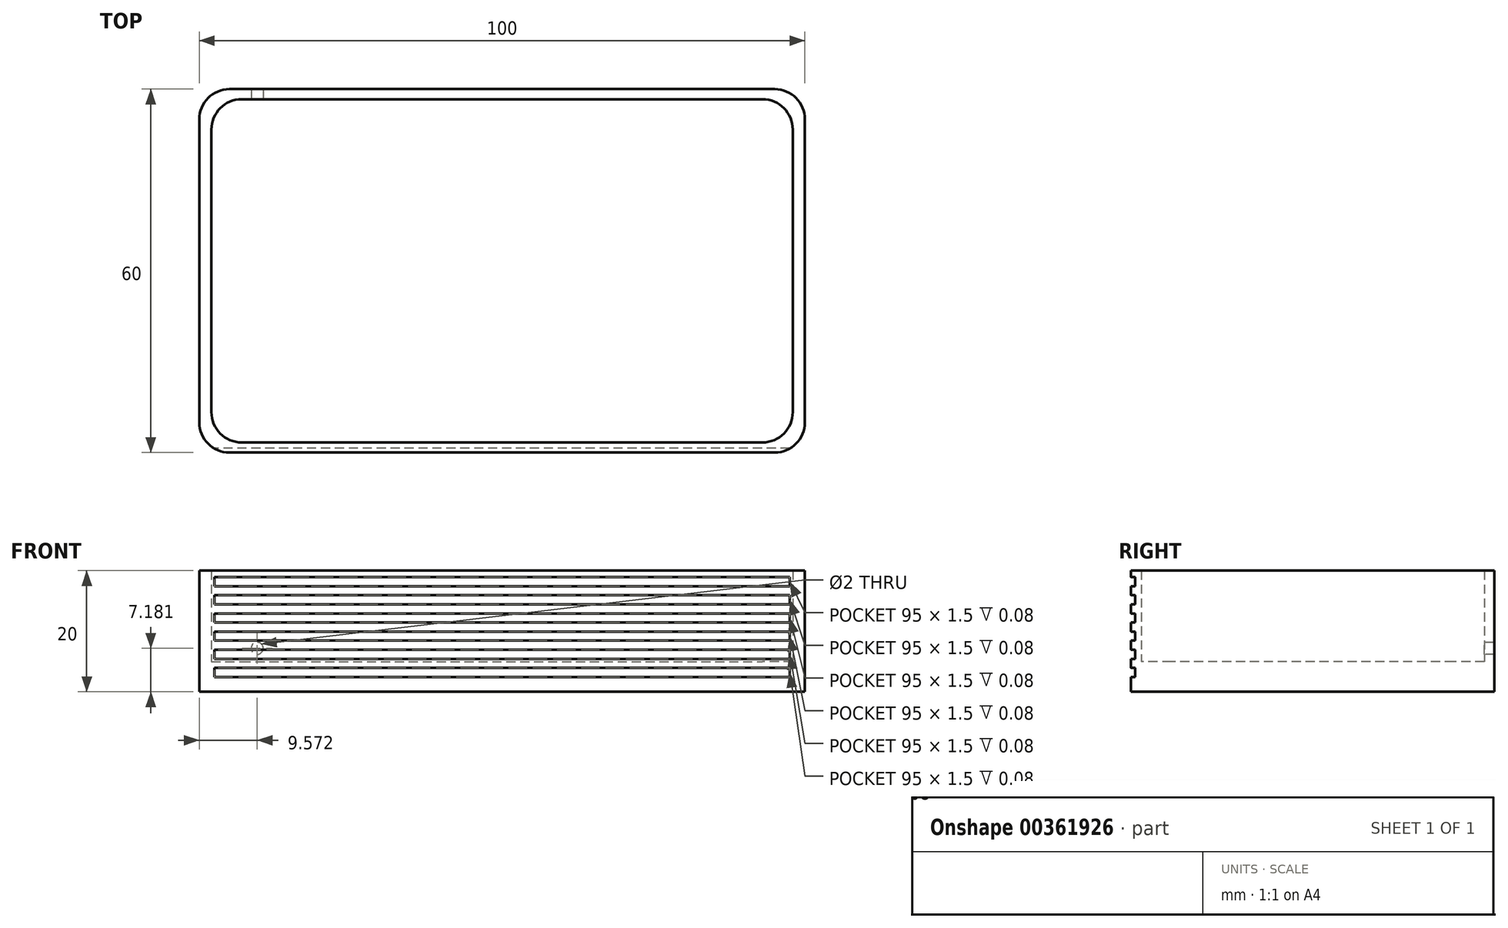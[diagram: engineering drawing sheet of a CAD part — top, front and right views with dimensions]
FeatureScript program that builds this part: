
annotation { "Feature Type Name" : "Feature", "Feature Type Description" : "" }
export const myFeature = defineFeature(function(context is Context, id is Id, definition is map)
    precondition{}
    {
        {
            var Q0;
            Q0=qCreatedBy(makeId("Top.planeOp"),FACE);
            var sketch = newSketch(context, id + "F0", { "sketchPlane" : qUnion([Q0])});
            skPoint(sketch, "E0.middle", {"position": v(0, 0) * mm});
            skLineSegment(sketch, "E1.bottom", {"start": v(45, -30) * mm, "end": v(-45, -30) * mm});
            skLineSegment(sketch, "E1.top", {"start": v(45, 30) * mm, "end": v(-45, 30) * mm});
            skLineSegment(sketch, "E1.left", {"start": v(50, -25) * mm, "end": v(50, 25) * mm});
            skLineSegment(sketch, "E1.right", {"start": v(-50, -25) * mm, "end": v(-50, 25) * mm});
            skLineSegment(sketch, "E2.bottom", {"start": v(-43, 28.33) * mm, "end": v(43, 28.33) * mm});
            skLineSegment(sketch, "E2.top", {"start": v(-43, -28.33) * mm, "end": v(43, -28.33) * mm});
            skLineSegment(sketch, "E2.left", {"start": v(-48, 23.33) * mm, "end": v(-48, -23.33) * mm});
            skLineSegment(sketch, "E2.right", {"start": v(48, 23.33) * mm, "end": v(48, -23.33) * mm});
            skPoint(sketch, "E3.visualSharp", {"position": v(-48, 28.33) * mm});
            skArc(sketch, "E3.filletArc", {"start": v(-43, 28.33) * mm, "mid": v(-46.54, 26.86) * mm, "end": v(-48, 23.33) * mm});
            skPoint(sketch, "E4.visualSharp", {"position": v(-50, 30) * mm});
            skArc(sketch, "E4.filletArc", {"start": v(-45, 30) * mm, "mid": v(-48.54, 28.54) * mm, "end": v(-50, 25) * mm});
            skPoint(sketch, "E5.visualSharp", {"position": v(-48, -28.33) * mm});
            skArc(sketch, "E5.filletArc", {"start": v(-48, -23.33) * mm, "mid": v(-46.54, -26.86) * mm, "end": v(-43, -28.33) * mm});
            skPoint(sketch, "E6.visualSharp", {"position": v(-50, -30) * mm});
            skArc(sketch, "E6.filletArc", {"start": v(-50, -25) * mm, "mid": v(-48.54, -28.54) * mm, "end": v(-45, -30) * mm});
            skPoint(sketch, "E7.visualSharp", {"position": v(48, -28.33) * mm});
            skArc(sketch, "E7.filletArc", {"start": v(43, -28.33) * mm, "mid": v(46.54, -26.86) * mm, "end": v(48, -23.33) * mm});
            skPoint(sketch, "E8.visualSharp", {"position": v(50, -30) * mm});
            skArc(sketch, "E8.filletArc", {"start": v(45, -30) * mm, "mid": v(48.54, -28.54) * mm, "end": v(50, -25) * mm});
            skPoint(sketch, "E9.visualSharp", {"position": v(50, 30) * mm});
            skArc(sketch, "E9.filletArc", {"start": v(50, 25) * mm, "mid": v(48.54, 28.54) * mm, "end": v(45, 30) * mm});
            skPoint(sketch, "E10.visualSharp", {"position": v(48, 28.33) * mm});
            skArc(sketch, "E10.filletArc", {"start": v(48, 23.33) * mm, "mid": v(46.54, 26.86) * mm, "end": v(43, 28.33) * mm});
            skSolve(sketch);
        }
        {
            var Q0;
            Q0=makeQuery(id+"F0.imprint","IMPRINT",FACE,{"disambiguationData":[TD([[makeQuery(id+"F0.imprint","IMPRINT",EDGE,{"derivedFrom":sQuery(id+"F0.wireOp",EDGE,"E1.bottom")}),-1.0]])]});
            extrude(context, id + "F1", {"entities" : qUnion([Q0]), "depth" : 20 * mm});
        }
        {
            var Q0;
            Q0=makeQuery(id+"F0.imprint","IMPRINT",FACE,{"disambiguationData":[TD([[makeQuery(id+"F0.imprint","IMPRINT",EDGE,{"derivedFrom":sQuery(id+"F0.wireOp",EDGE,"E2.bottom")}),-1.0]])]});
            extrude(context, id + "F2", {"entities" : qUnion([Q0]), "operationType" : NewBodyOperationType.ADD, "depth" : 5 * mm});
        }
        {
            var Q0;
            Q0=makeQuery(id+"F1.opExtrude","SWEPT_FACE",FACE,{"disambiguationData":[OSD([sQuery(id+"F0.wireOp",EDGE,"E1.bottom")])]});
            var sketch = newSketch(context, id + "F3", { "sketchPlane" : qUnion([Q0])});
            skLineSegment(sketch, "E11.bottom", {"start": v(47.5, 2.45) * mm, "end": v(-47.5, 2.45) * mm});
            skLineSegment(sketch, "E11.top", {"start": v(47.5, 3.95) * mm, "end": v(-47.5, 3.95) * mm});
            skLineSegment(sketch, "E11.left", {"start": v(47.5, 2.45) * mm, "end": v(47.5, 3.95) * mm});
            skLineSegment(sketch, "E11.right", {"start": v(-47.5, 2.45) * mm, "end": v(-47.5, 3.95) * mm});
            skPoint(sketch, "E11.middle", {"position": v(0, 3.2) * mm});
            skLineSegment(sketch, "E12.0.1.0", {"start": v(-47.5, 5.45) * mm, "end": v(-47.5, 6.95) * mm});
            skLineSegment(sketch, "E12.0.1.1", {"start": v(47.5, 5.45) * mm, "end": v(-47.5, 5.45) * mm});
            skLineSegment(sketch, "E12.0.1.2", {"start": v(47.5, 6.95) * mm, "end": v(-47.5, 6.95) * mm});
            skLineSegment(sketch, "E12.0.1.3", {"start": v(47.5, 5.45) * mm, "end": v(47.5, 6.95) * mm});
            skLineSegment(sketch, "E12.0.2.0", {"start": v(-47.5, 8.45) * mm, "end": v(-47.5, 9.95) * mm});
            skLineSegment(sketch, "E12.0.2.1", {"start": v(47.5, 8.45) * mm, "end": v(-47.5, 8.45) * mm});
            skLineSegment(sketch, "E12.0.2.2", {"start": v(47.5, 9.95) * mm, "end": v(-47.5, 9.95) * mm});
            skLineSegment(sketch, "E12.0.2.3", {"start": v(47.5, 8.45) * mm, "end": v(47.5, 9.95) * mm});
            skLineSegment(sketch, "E12.0.3.0", {"start": v(-47.5, 11.45) * mm, "end": v(-47.5, 12.95) * mm});
            skLineSegment(sketch, "E12.0.3.1", {"start": v(47.5, 11.45) * mm, "end": v(-47.5, 11.45) * mm});
            skLineSegment(sketch, "E12.0.3.2", {"start": v(47.5, 12.95) * mm, "end": v(-47.5, 12.95) * mm});
            skLineSegment(sketch, "E12.0.3.3", {"start": v(47.5, 11.45) * mm, "end": v(47.5, 12.95) * mm});
            skLineSegment(sketch, "E12.0.4.0", {"start": v(-47.5, 14.45) * mm, "end": v(-47.5, 15.95) * mm});
            skLineSegment(sketch, "E12.0.4.1", {"start": v(47.5, 14.45) * mm, "end": v(-47.5, 14.45) * mm});
            skLineSegment(sketch, "E12.0.4.2", {"start": v(47.5, 15.95) * mm, "end": v(-47.5, 15.95) * mm});
            skLineSegment(sketch, "E12.0.4.3", {"start": v(47.5, 14.45) * mm, "end": v(47.5, 15.95) * mm});
            skLineSegment(sketch, "E12.0.5.0", {"start": v(-47.5, 17.45) * mm, "end": v(-47.5, 18.95) * mm});
            skLineSegment(sketch, "E12.0.5.1", {"start": v(47.5, 17.45) * mm, "end": v(-47.5, 17.45) * mm});
            skLineSegment(sketch, "E12.0.5.2", {"start": v(47.5, 18.95) * mm, "end": v(-47.5, 18.95) * mm});
            skLineSegment(sketch, "E12.0.5.3", {"start": v(47.5, 17.45) * mm, "end": v(47.5, 18.95) * mm});
            skLineSegment(sketch, "E12.direction1", {"start": v(-47.5, 2.45) * mm, "end": v(-22.5, 2.45) * mm, "construction": true});
            skLineSegment(sketch, "E12.direction2", {"start": v(-47.5, 2.45) * mm, "end": v(-47.5, 5.45) * mm, "construction": true});
            skSolve(sketch);
        }
        {
            var Q0;
            Q0 = qSketchRegion(id + "F3", true);
            extrude(context, id + "F4", {"entities" : qUnion([Q0]), "operationType" : NewBodyOperationType.REMOVE, "oppositeDirection" : true, "depth" : 0.75 * mm});
        }
        {
            var Q0;
            Q0=makeQuery(id+"F1.opExtrude","SWEPT_FACE",FACE,{"disambiguationData":[OSD([sQuery(id+"F0.wireOp",EDGE,"E2.bottom")])]});
            var sketch = newSketch(context, id + "F5", { "sketchPlane" : qUnion([Q0])});
            skCircle(sketch, "E13", {"center": v(-40.43, 7.18) * mm, "radius": 1 * mm});
            skSolve(sketch);
        }
        {
            var Q0;
            Q0 = qSketchRegion(id + "F5", true);
            var Q1;
            Q1=sQuery(id+"F5.wireOp",EDGE,"E13");
            extrude(context, id + "F6", {"entities" : qUnion([Q0]), "operationType" : NewBodyOperationType.REMOVE, "surfaceEntities" : qUnion([Q1]), "oppositeDirection" : true, "depth" : 25 * mm});
        }
    });
